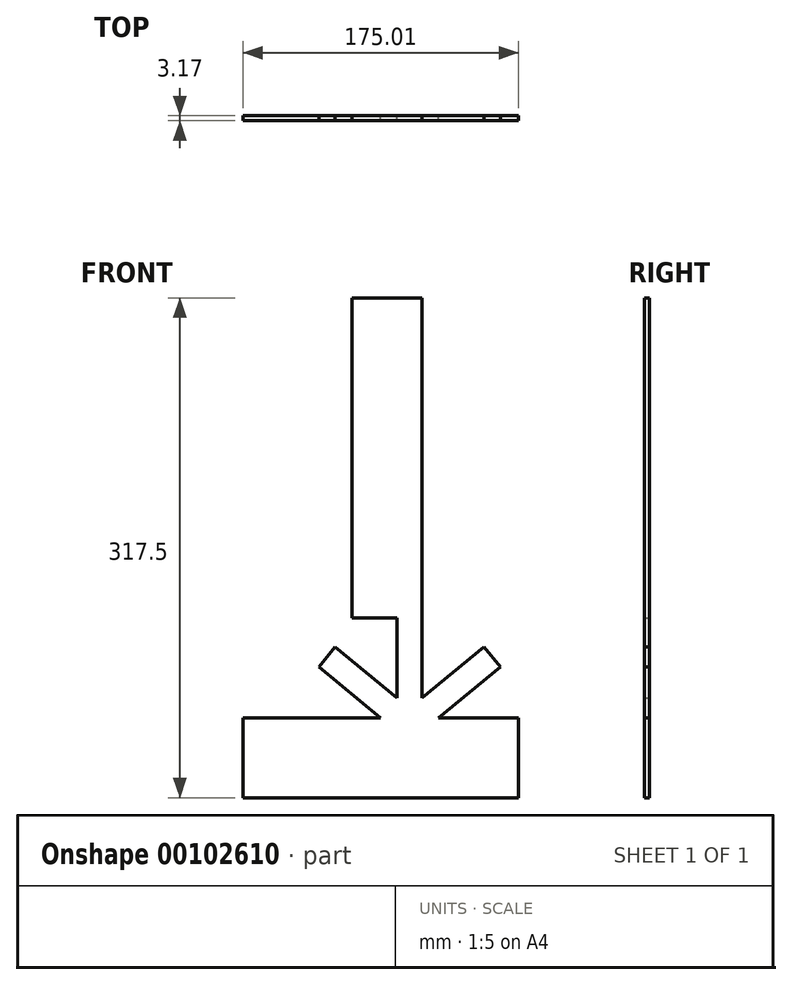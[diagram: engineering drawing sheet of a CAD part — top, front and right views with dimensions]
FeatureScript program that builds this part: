
annotation { "Feature Type Name" : "Feature", "Feature Type Description" : "" }
export const myFeature = defineFeature(function(context is Context, id is Id, definition is map)
    precondition{}
    {
        {
            var Q0;
            Q0=qCreatedBy(makeId("Front.planeOp"),FACE);
            var sketch = newSketch(context, id + "F0", { "sketchPlane" : qUnion([Q0])});
            skLineSegment(sketch, "E0.bottom", {"start": v(22.23, 101.6) * mm, "end": v(-22.23, 101.6) * mm});
            skLineSegment(sketch, "E0.left", {"start": v(22.23, 101.6) * mm, "end": v(22.23, -101.6) * mm});
            skLineSegment(sketch, "E0.right", {"start": v(-22.23, 101.6) * mm, "end": v(-22.23, -101.6) * mm});
            skPoint(sketch, "E0.middle", {"position": v(0, 0) * mm});
            skLineSegment(sketch, "E1", {"start": v(6.35, 101.6) * mm, "end": v(6.35, -101.6) * mm, "construction": true});
            skLineSegment(sketch, "E2", {"start": v(-6.35, 101.6) * mm, "end": v(-6.35, -101.6) * mm, "construction": true});
            skLineSegment(sketch, "E3.top", {"start": v(6.35, -152.4) * mm, "end": v(22.23, -152.4) * mm, "construction": true});
            skLineSegment(sketch, "E3.left", {"start": v(6.35, -101.6) * mm, "end": v(6.35, -152.4) * mm});
            skLineSegment(sketch, "E3.right", {"start": v(22.23, -101.6) * mm, "end": v(22.23, -152.4) * mm});
            skLineSegment(sketch, "E4", {"start": v(32.64, -215.9) * mm, "end": v(32.64, -165.1) * mm, "construction": true});
            skLineSegment(sketch, "E5", {"start": v(32.64, -165.1) * mm, "end": v(22.22, -152.4) * mm, "construction": true});
            skLineSegment(sketch, "E6", {"start": v(22.23, -152.4) * mm, "end": v(61.5, -120.19) * mm});
            skLineSegment(sketch, "E7", {"start": v(32.64, -165.1) * mm, "end": v(71.92, -132.89) * mm});
            skLineSegment(sketch, "E8", {"start": v(71.92, -132.89) * mm, "end": v(61.5, -120.19) * mm});
            skLineSegment(sketch, "E9", {"start": v(32.64, -165.1) * mm, "end": v(83.44, -165.1) * mm});
            skLineSegment(sketch, "E10", {"start": v(83.44, -165.1) * mm, "end": v(83.44, -215.9) * mm});
            skLineSegment(sketch, "E11", {"start": v(83.44, -215.9) * mm, "end": v(32.64, -215.9) * mm});
            skLineSegment(sketch, "E12", {"start": v(-22.23, -101.6) * mm, "end": v(-6.35, -101.6) * mm});
            skLineSegment(sketch, "E13", {"start": v(-6.35, -101.6) * mm, "end": v(6.35, -101.6) * mm});
            skPoint(sketch, "E14", {"position": v(14.29, -152.4) * mm});
            skLineSegment(sketch, "E15", {"start": v(14.29, -152.4) * mm, "end": v(14.29, -323.83) * mm, "construction": true});
            skLineSegment(sketch, "E16", {"start": v(32.64, -215.9) * mm, "end": v(14.29, -215.9) * mm});
            skLineSegment(sketch, "E17", {"start": v(22.23, -152.4) * mm, "end": v(22.23, -165.1) * mm, "construction": true});
            skLineSegment(sketch, "E18", {"start": v(32.64, -165.1) * mm, "end": v(22.23, -165.1) * mm, "construction": true});
            skLineSegment(sketch, "E19.MirrorCS", {"start": v(-4.06, -215.9) * mm, "end": v(14.29, -215.9) * mm});
            skLineSegment(sketch, "E20.MirrorCS", {"start": v(-54.86, -215.9) * mm, "end": v(-4.06, -215.9) * mm});
            skLineSegment(sketch, "E21.MirrorCS", {"start": v(-54.86, -165.1) * mm, "end": v(-54.86, -215.9) * mm});
            skLineSegment(sketch, "E22.MirrorCS", {"start": v(-4.06, -165.1) * mm, "end": v(-54.86, -165.1) * mm});
            skLineSegment(sketch, "E23.MirrorCS", {"start": v(-4.06, -165.1) * mm, "end": v(-43.35, -132.89) * mm});
            skLineSegment(sketch, "E24.MirrorCS", {"start": v(6.35, -152.4) * mm, "end": v(-32.93, -120.19) * mm});
            skLineSegment(sketch, "E25.MirrorCS", {"start": v(-43.35, -132.89) * mm, "end": v(-32.93, -120.19) * mm});
            skLineSegment(sketch, "E26", {"start": v(-54.86, -165.1) * mm, "end": v(-91.57, -165.1) * mm});
            skLineSegment(sketch, "E27", {"start": v(-91.57, -165.1) * mm, "end": v(-91.57, -215.9) * mm});
            skLineSegment(sketch, "E28", {"start": v(-91.57, -215.9) * mm, "end": v(-54.86, -215.9) * mm});
            skSolve(sketch);
        }
        {
            var Q0;
            Q0 = qSketchRegion(id + "F0", true);
            extrude(context, id + "F1", {"entities" : qUnion([Q0]), "depth" : 3.17 * mm});
        }
    });
